# Revit family: Lockin Lockers AU_Shelving Locker_R22
name_source: partatom
category: Furniture
units: mm (PartAtom-declared; Revit-internal decimal feet)

## family parameters
Always vertical = Yes
Cut with Voids When Loaded = No
OmniClass Number = 23.40.20.27
OmniClass Title = Storage Shelving
Render Appearance Source = Family Geometry
Room Calculation Point = No
Shared = Yes
Work Plane-Based = Yes

## types (4) — shared parameters
Base Height Control = 100 mm  [stored 0.328084 ft]
Body/Frame Material = Material - Melamine - Laminex or Polytec Finish
Depth Control = 500 mm  [stored 1.64042 ft]
Desired Base Height = 100 mm  [stored 0.328084 ft]
Desired Depth = 500 mm  [stored 1.64042 ft]
Desired Height = 1900 mm  [stored 6.2336 ft]
Desired Width = 400 mm  [stored 1.31234 ft]
Door Material = Material - Melamine - Laminex or Polytec Finish
Door Type = Lockin_Locker Door_Standard_R22 : Standard Door/Combination Lock
Height Control = 1900 mm  [stored 6.2336 ft]
Locker Joint = 3 mm  [stored 0.00984252 ft]
Manufacturer = Lockin Lockers AU
Maximum Base Height = 450 mm  [stored 1.47638 ft]
Maximum Depth = 600 mm
Maximum Height = 2100 mm
Maximum Width = 600 mm
Minimum Base Height = 80 mm  [stored 0.262467 ft]
Minimum Depth = 200 mm  [stored 0.656168 ft]
Minimum Height = 1800 mm  [stored 5.90551 ft]
Minimum Width = 300 mm
Offfset Cubby = 180 mm  [stored 0.590551 ft]
TH Wall = 18 mm  [stored 0.0590551 ft]
URL = https://www.lockin.com.au
Width Control = 400 mm  [stored 1.31234 ft]
zero-valued in all types: Default Elevation

## per-type parameters (varying)
| type | Description | H Locker | Model | N_Doors | N_Shelves | vis_Cubby 1 | vis_Cubby 2 | vis_Cubby 3 | vis_Cubby 4 |
| Shelving Locker 2 door (H2) | Shelving Locker 2 door | 898.5 mm  [stored 2.94783 ft] | H2 | 2 | 2 | Yes | Yes | No | No |
| Shelving Locker 3 door (H3) | Shelving Locker 3 door | 598 mm  [stored 1.96194 ft] | H3 | 3 | 3 | Yes | Yes | Yes | No |
| Shelving Locker 4 door (H4) | Shelving Locker 4 door | 447.75 mm  [stored 1.469 ft] | H4 | 4 | 4 | Yes | Yes | Yes | Yes |
| Shelving Locker 5 door (H5) | Shelving Locker 5 door | 357.6 mm  [stored 1.17323 ft] | H5 | 5 | 5 | No | No | No | No |

note: [stored X ft] marks values corroborated as IEEE doubles in the binary element streams (Revit-internal decimal feet)

## geometry (parser evidence)
native form markers: Sweep x2
no freeform markers — native parametric forms only
